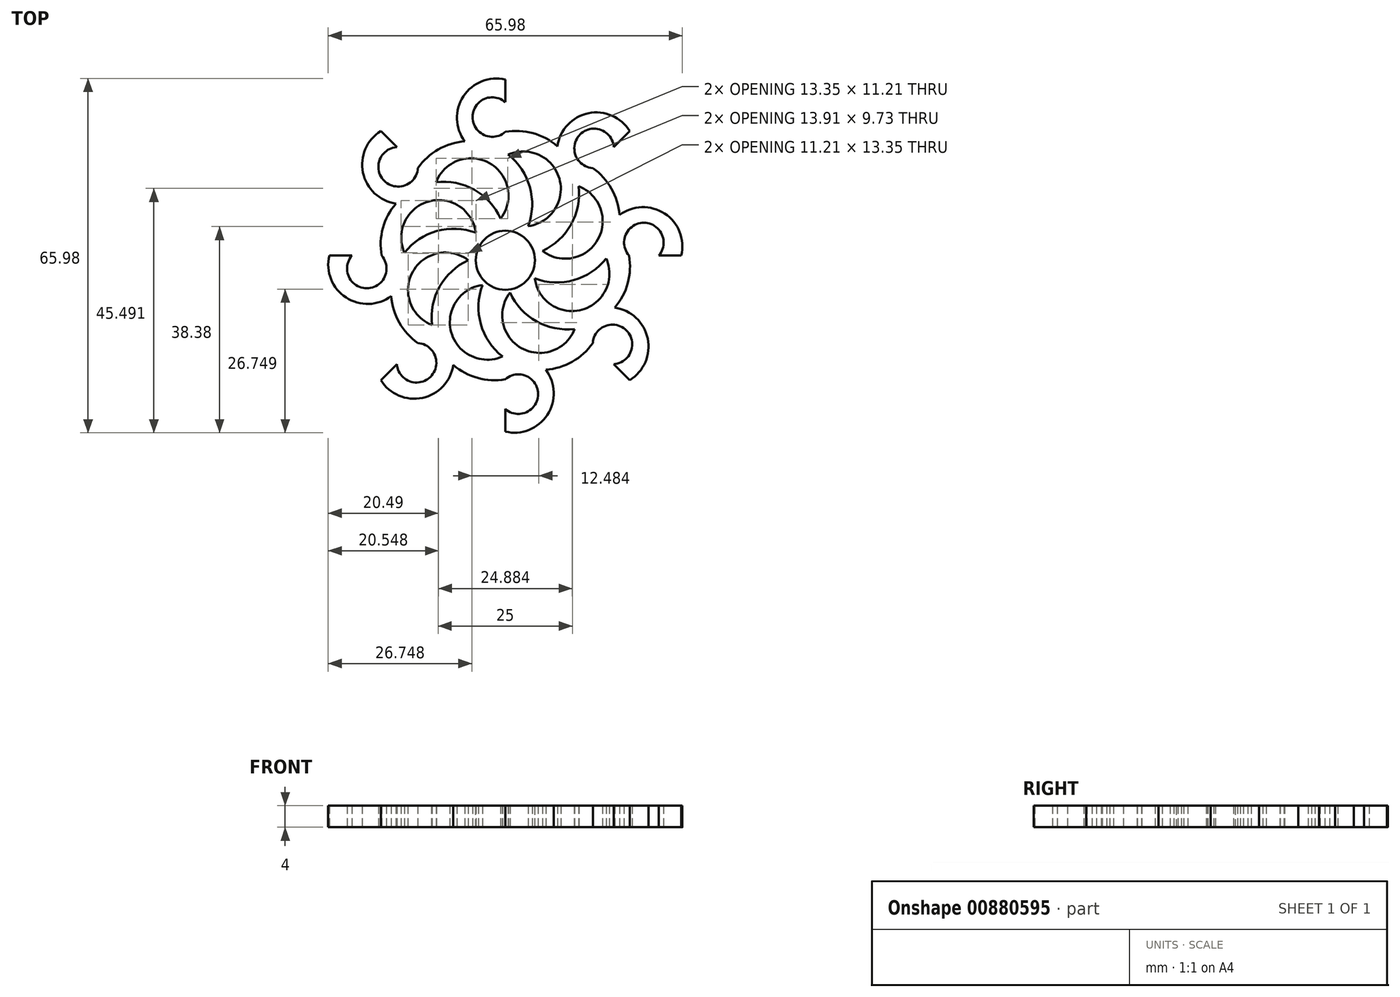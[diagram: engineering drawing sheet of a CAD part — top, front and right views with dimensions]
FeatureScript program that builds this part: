
annotation { "Feature Type Name" : "Feature", "Feature Type Description" : "" }
export const myFeature = defineFeature(function(context is Context, id is Id, definition is map)
    precondition{}
    {
        {
            var Q0;
            Q0=qCreatedBy(makeId("Top.planeOp"),FACE);
            var sketch = newSketch(context, id + "F0", { "sketchPlane" : qUnion([Q0])});
            skArc(sketch, "E0", {"start": v(0, 26.5) * mm, "mid": v(-9.02, 19.38) * mm, "end": v(0, 12.25) * mm});
            skArc(sketch, "E1", {"start": v(0, 0) * mm, "mid": v(10.34, 6.12) * mm, "end": v(0, 12.25) * mm});
            skLineSegment(sketch, "E2", {"start": v(0, 26.5) * mm, "end": v(0, 22.29) * mm});
            skArc(sketch, "E3", {"start": v(0, 22.29) * mm, "mid": v(-6.1, 19.52) * mm, "end": v(0, 16.75) * mm});
            skArc(sketch, "E4", {"start": v(0, -6.29) * mm, "mid": v(13.75, 5.23) * mm, "end": v(0, 16.75) * mm});
            skLineSegment(sketch, "E5", {"start": v(0, 0) * mm, "end": v(0, -6.29) * mm});
            skSolve(sketch);
        }
        {
            var Q0;
            Q0=makeQuery(id+"F0.imprint","IMPRINT",FACE,{"disambiguationData":[TD([[makeQuery(id+"F0.imprint","IMPRINT",EDGE,{"derivedFrom":sQuery(id+"F0.wireOp",EDGE,"E0")}),1.0]])]});
            extrude(context, id + "F1", {"entities" : qUnion([Q0]), "depth" : 4 * mm, "offsetDistance" : 25.4 * mm});
        }
        {
            var Q0;
            Q0=makeQuery(id+"F1.opExtrude","SWEPT_BODY",BODY,{"disambiguationData":[OSD([sQuery(id+"F0.wireOp",EDGE,"E0"),sQuery(id+"F0.wireOp",EDGE,"E1"),sQuery(id+"F0.wireOp",EDGE,"E2"),sQuery(id+"F0.wireOp",EDGE,"E3"),sQuery(id+"F0.wireOp",EDGE,"E4"),sQuery(id+"F0.wireOp",EDGE,"E5")])]});
            var Q1;
            Q1=makeQuery(id+"F1.opExtrude","SWEPT_EDGE",EDGE,{"disambiguationData":[OSD([sQuery(id+"F0.wireOp",EDGE,"E4"),sQuery(id+"F0.wireOp",EDGE,"E5")])]});
            circularPattern(context, id + "F2", {"entities" : qUnion([Q0]), "axis" : qUnion([Q1]), "angle" : 360 * degree, "instanceCount" : 8, "equalSpace" : true});
        }
        {
            var Q0;
            Q0=makeQuery(id+"F2.opPattern","COPY",BODY,{"derivedFrom":makeQuery(id+"F1.opExtrude","SWEPT_BODY",BODY,{"disambiguationData":[OSD([sQuery(id+"F0.wireOp",EDGE,"E0"),sQuery(id+"F0.wireOp",EDGE,"E1"),sQuery(id+"F0.wireOp",EDGE,"E2"),sQuery(id+"F0.wireOp",EDGE,"E3"),sQuery(id+"F0.wireOp",EDGE,"E4"),sQuery(id+"F0.wireOp",EDGE,"E5")])]}),"instanceName":"6"});
            var Q1;
            Q1=makeQuery(id+"F2.opPattern","COPY",BODY,{"derivedFrom":makeQuery(id+"F1.opExtrude","SWEPT_BODY",BODY,{"disambiguationData":[OSD([sQuery(id+"F0.wireOp",EDGE,"E0"),sQuery(id+"F0.wireOp",EDGE,"E1"),sQuery(id+"F0.wireOp",EDGE,"E2"),sQuery(id+"F0.wireOp",EDGE,"E3"),sQuery(id+"F0.wireOp",EDGE,"E4"),sQuery(id+"F0.wireOp",EDGE,"E5")])]}),"instanceName":"7"});
            var Q2;
            Q2=makeQuery(id+"F2.opPattern","COPY",BODY,{"derivedFrom":makeQuery(id+"F1.opExtrude","SWEPT_BODY",BODY,{"disambiguationData":[OSD([sQuery(id+"F0.wireOp",EDGE,"E0"),sQuery(id+"F0.wireOp",EDGE,"E1"),sQuery(id+"F0.wireOp",EDGE,"E2"),sQuery(id+"F0.wireOp",EDGE,"E3"),sQuery(id+"F0.wireOp",EDGE,"E4"),sQuery(id+"F0.wireOp",EDGE,"E5")])]}),"instanceName":"5"});
            var Q3;
            Q3=makeQuery(id+"F2.opPattern","COPY",BODY,{"derivedFrom":makeQuery(id+"F1.opExtrude","SWEPT_BODY",BODY,{"disambiguationData":[OSD([sQuery(id+"F0.wireOp",EDGE,"E0"),sQuery(id+"F0.wireOp",EDGE,"E1"),sQuery(id+"F0.wireOp",EDGE,"E2"),sQuery(id+"F0.wireOp",EDGE,"E3"),sQuery(id+"F0.wireOp",EDGE,"E4"),sQuery(id+"F0.wireOp",EDGE,"E5")])]}),"instanceName":"2"});
            var Q4;
            Q4=makeQuery(id+"F2.opPattern","COPY",BODY,{"derivedFrom":makeQuery(id+"F1.opExtrude","SWEPT_BODY",BODY,{"disambiguationData":[OSD([sQuery(id+"F0.wireOp",EDGE,"E0"),sQuery(id+"F0.wireOp",EDGE,"E1"),sQuery(id+"F0.wireOp",EDGE,"E2"),sQuery(id+"F0.wireOp",EDGE,"E3"),sQuery(id+"F0.wireOp",EDGE,"E4"),sQuery(id+"F0.wireOp",EDGE,"E5")])]}),"instanceName":"1"});
            var Q5;
            Q5=makeQuery(id+"F2.opPattern","COPY",BODY,{"derivedFrom":makeQuery(id+"F1.opExtrude","SWEPT_BODY",BODY,{"disambiguationData":[OSD([sQuery(id+"F0.wireOp",EDGE,"E0"),sQuery(id+"F0.wireOp",EDGE,"E1"),sQuery(id+"F0.wireOp",EDGE,"E2"),sQuery(id+"F0.wireOp",EDGE,"E3"),sQuery(id+"F0.wireOp",EDGE,"E4"),sQuery(id+"F0.wireOp",EDGE,"E5")])]}),"instanceName":"4"});
            var Q6;
            Q6=makeQuery(id+"F2.opPattern","COPY",BODY,{"derivedFrom":makeQuery(id+"F1.opExtrude","SWEPT_BODY",BODY,{"disambiguationData":[OSD([sQuery(id+"F0.wireOp",EDGE,"E0"),sQuery(id+"F0.wireOp",EDGE,"E1"),sQuery(id+"F0.wireOp",EDGE,"E2"),sQuery(id+"F0.wireOp",EDGE,"E3"),sQuery(id+"F0.wireOp",EDGE,"E4"),sQuery(id+"F0.wireOp",EDGE,"E5")])]}),"instanceName":"3"});
            var Q7;
            Q7=makeQuery(id+"F1.opExtrude","SWEPT_BODY",BODY,{"disambiguationData":[OSD([sQuery(id+"F0.wireOp",EDGE,"E0"),sQuery(id+"F0.wireOp",EDGE,"E1"),sQuery(id+"F0.wireOp",EDGE,"E2"),sQuery(id+"F0.wireOp",EDGE,"E3"),sQuery(id+"F0.wireOp",EDGE,"E4"),sQuery(id+"F0.wireOp",EDGE,"E5")])]});
            booleanBodies(context, id + "F3", {"operationType" : BooleanOperationType.UNION, "tools" : qUnion([Q0, Q1, Q2, Q3, Q4, Q5, Q6, Q7])});
        }
        {
            var Q0;
            {var subQ0=makeQuery(id+"F1.opExtrude","CAP_FACE",FACE,{"disambiguationData":[OSD([sQuery(id+"F0.wireOp",EDGE,"E0"),sQuery(id+"F0.wireOp",EDGE,"E1"),sQuery(id+"F0.wireOp",EDGE,"E2"),sQuery(id+"F0.wireOp",EDGE,"E3"),sQuery(id+"F0.wireOp",EDGE,"E4"),sQuery(id+"F0.wireOp",EDGE,"E5")])],"isStart":false});Q0=makeQuery(id+"F3.opBoolean","MERGE",FACE,{"derivedFrom":[subQ0,makeQuery(id+"F2.opPattern","COPY",FACE,{"derivedFrom":subQ0,"instanceName":"1"}),makeQuery(id+"F2.opPattern","COPY",FACE,{"derivedFrom":subQ0,"instanceName":"2"}),makeQuery(id+"F2.opPattern","COPY",FACE,{"derivedFrom":subQ0,"instanceName":"3"}),makeQuery(id+"F2.opPattern","COPY",FACE,{"derivedFrom":subQ0,"instanceName":"4"}),makeQuery(id+"F2.opPattern","COPY",FACE,{"derivedFrom":subQ0,"instanceName":"5"}),makeQuery(id+"F2.opPattern","COPY",FACE,{"derivedFrom":subQ0,"instanceName":"6"}),makeQuery(id+"F2.opPattern","COPY",FACE,{"derivedFrom":subQ0,"instanceName":"7"})]});}
            var sketch = newSketch(context, id + "F4", { "sketchPlane" : qUnion([Q0])});
            skCircle(sketch, "E6", {"center": v(0, -7.16) * mm, "radius": 5.5 * mm});
            skSolve(sketch);
        }
        {
            var Q0;
            Q0=makeQuery(id+"F4.imprint","IMPRINT",FACE,{"disambiguationData":[TD([[makeQuery(id+"F4.imprint","IMPRINT",EDGE,{"derivedFrom":sQuery(id+"F4.wireOp",EDGE,"E6")}),1.0]])]});
            var Q1;
            Q1=sQuery(id+"F4.wireOp",EDGE,"E6");
            extrude(context, id + "F5", {"entities" : qUnion([Q0]), "operationType" : NewBodyOperationType.REMOVE, "surfaceEntities" : qUnion([Q1]), "oppositeDirection" : true, "depth" : 4 * mm, "offsetDistance" : 25.4 * mm});
        }
    });
